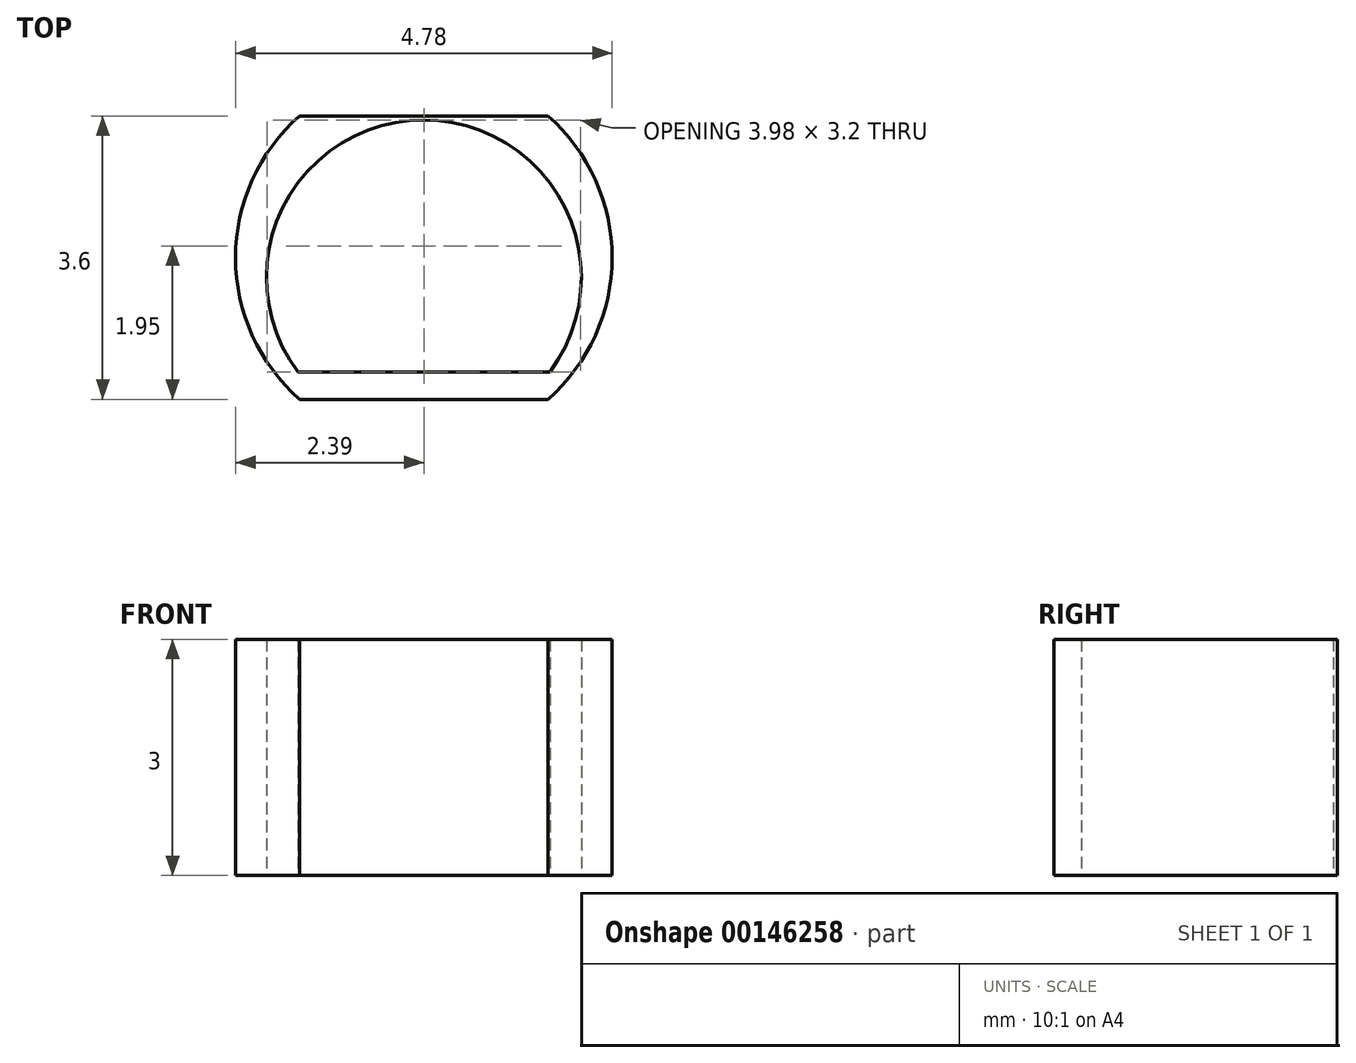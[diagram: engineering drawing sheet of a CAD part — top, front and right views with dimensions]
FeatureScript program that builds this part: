
annotation { "Feature Type Name" : "Feature", "Feature Type Description" : "" }
export const myFeature = defineFeature(function(context is Context, id is Id, definition is map)
    precondition{}
    {
        {
            var Q0;
            Q0=qCreatedBy(makeId("Top.planeOp"),FACE);
            var sketch = newSketch(context, id + "F0", { "sketchPlane" : qUnion([Q0])});
            skLineSegment(sketch, "E0", {"start": v(0, 0) * mm, "end": v(-2.5, 0) * mm, "construction": true});
            skLineSegment(sketch, "E1", {"start": v(-2.5, 0) * mm, "end": v(2.4, 0) * mm, "construction": true});
            skArc(sketch, "E2", {"start": v(1.58, -1.8) * mm, "mid": v(2.4, 0) * mm, "end": v(1.58, 1.8) * mm});
            skLineSegment(sketch, "E3", {"start": v(0, 0) * mm, "end": v(0, 1.8) * mm, "construction": true});
            skLineSegment(sketch, "E4", {"start": v(0, 0) * mm, "end": v(0, -1.8) * mm, "construction": true});
            skLineSegment(sketch, "E5", {"start": v(0, -1.8) * mm, "end": v(1.58, -1.8) * mm});
            skLineSegment(sketch, "E6", {"start": v(1.58, -1.8) * mm, "end": v(-1.58, -1.8) * mm});
            skLineSegment(sketch, "E7", {"start": v(0, 1.8) * mm, "end": v(1.58, 1.8) * mm});
            skLineSegment(sketch, "E8", {"start": v(0, 1.8) * mm, "end": v(-1.58, 1.8) * mm});
            skArc(sketch, "E9.trimOffspring", {"start": v(-1.58, 1.8) * mm, "mid": v(-2.4, 0) * mm, "end": v(-1.58, -1.8) * mm});
            skArc(sketch, "E10", {"start": v(2, -0.13) * mm, "mid": v(2, -0.06) * mm, "end": v(2, 0) * mm});
            skPoint(sketch, "E11", {"position": v(0, 2) * mm});
            skLineSegment(sketch, "E12", {"start": v(0, 2) * mm, "end": v(0, -1.3) * mm, "construction": true});
            skLineSegment(sketch, "E13", {"start": v(0, -1.8) * mm, "end": v(0, -1.45) * mm, "construction": true});
            skPoint(sketch, "E14", {"position": v(0, -1.45) * mm});
            skLineSegment(sketch, "E15", {"start": v(-1.6, -1.45) * mm, "end": v(1.6, -1.45) * mm});
            skLineSegment(sketch, "E16", {"start": v(0, 0) * mm, "end": v(0, -0.25) * mm, "construction": true});
            skArc(sketch, "E17", {"start": v(1.6, -1.45) * mm, "mid": v(0, 1.75) * mm, "end": v(-1.6, -1.45) * mm});
            skArc(sketch, "E18.trimOffspring", {"start": v(-2, 0) * mm, "mid": v(-2, -0.06) * mm, "end": v(-2, -0.12) * mm});
            skSolve(sketch);
        }
        {
            var Q0;
            {var subQ1=sQuery(id+"F0.wireOp",EDGE,"E2");Q0=makeQuery(id+"F0.imprint","IMPRINT",FACE,{"disambiguationData":[TD([[makeQuery(id+"F0.imprint","IMPRINT",EDGE,{"derivedFrom":subQ1}),1.0]])]});}
            extrude(context, id + "F1", {"entities" : qUnion([Q0]), "endBound" : BoundingType.SYMMETRIC, "depth" : 3 * mm});
        }
    });
